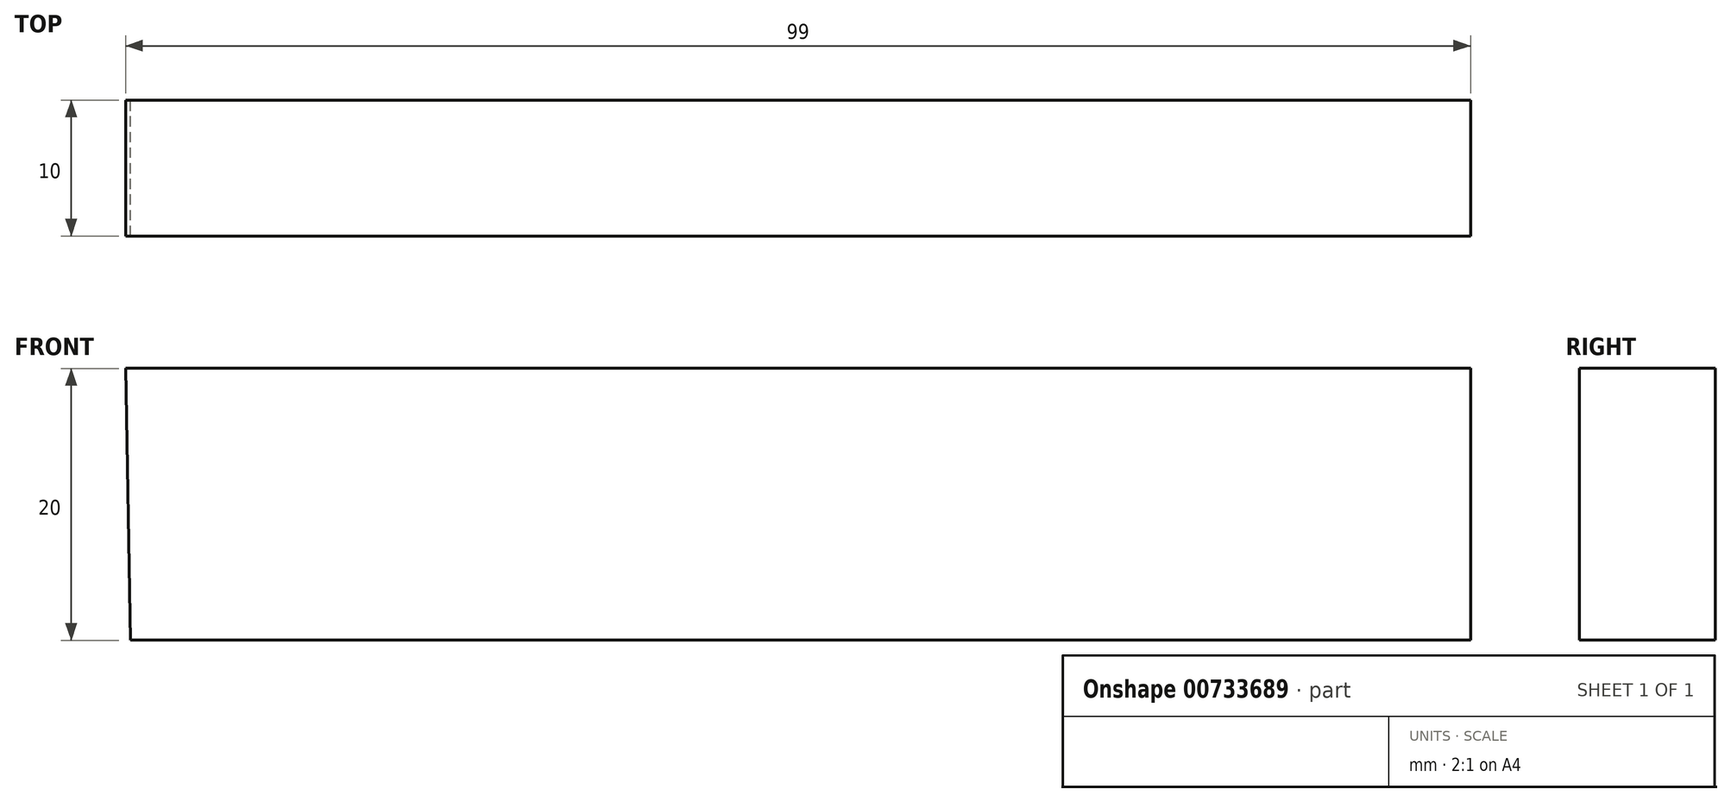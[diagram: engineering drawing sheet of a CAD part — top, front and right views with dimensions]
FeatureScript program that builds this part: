
annotation { "Feature Type Name" : "Feature", "Feature Type Description" : "" }
export const myFeature = defineFeature(function(context is Context, id is Id, definition is map)
    precondition{}
    {
        {
            var Q0;
            Q0=qCreatedBy(makeId("Front.planeOp"),FACE);
            var sketch = newSketch(context, id + "F0", { "sketchPlane" : qUnion([Q0])});
            skLineSegment(sketch, "E0", {"start": v(-99, 57.34) * mm, "end": v(0, 57.34) * mm});
            skLineSegment(sketch, "E1", {"start": v(0, 57.34) * mm, "end": v(-49.5, 57.34) * mm});
            skLineSegment(sketch, "E2", {"start": v(0, 57.34) * mm, "end": v(0, 37.34) * mm});
            skLineSegment(sketch, "E3", {"start": v(-98.64, 37.35) * mm, "end": v(-99, 57.34) * mm});
            skLineSegment(sketch, "E4", {"start": v(-98.64, 37.35) * mm, "end": v(0, 37.34) * mm});
            skSolve(sketch);
        }
        {
            var Q0;
            Q0=makeQuery(id+"F0.imprint","IMPRINT",FACE,{"disambiguationData":[TD([[makeQuery(id+"F0.imprint","IMPRINT",EDGE,{"derivedFrom":sQuery(id+"F0.wireOp",EDGE,"E0")}),-1.0]])]});
            var Q1;
            Q1 = qSketchRegion(id + "F0", true);
            extrude(context, id + "F1", {"entities" : qUnion([Q0, Q1]), "depth" : 10 * mm, "offsetDistance" : 25 * mm});
        }
    });
